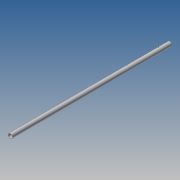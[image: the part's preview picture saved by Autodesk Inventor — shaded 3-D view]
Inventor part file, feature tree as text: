
AUTODESK INVENTOR PART (.ipt)
format: ipt  version: 2016 SP2 (Build 200236200, 236)  size: 98,816 bytes
history: native  units: in
note: dims shown in document units (in); Inventor stores cm internally (conversion verified against a paired STEP export)
features: sketch x3, extrude x2, hole x1
ambient origin geometry x8: Origin, YZ Plane, XZ Plane, XY Plane, X Axis, Y Axis, Z Axis, Center Point
bodies: Solid1 (feature_tree)
feature tree (6):
  extrude  "Extrusion1"  Depth=0.0638in
  extrude  "Extrusion3"  Depth=0.4134in
  hole  "Hole3"  [1 undecoded]
  sketch  "Sketch1"  dims[d0=0.8661in d2=0.0638in]
  sketch  "Sketch6"  dims[d3=29.8819in d4=0.0in d18=0.4134in]
  sketch  "Sketch7"  dims[d19=1.0in d20=0.0in d32=1.1811in d34=5.9055in d35=0.3937in d37=1.0in d39=0.125in d40=0.75in d41=0.375in d42=0.25in d43=0.5635in d44=1.0in d45=0.8108in d47=2.0472in d48=5.9055in]
note: 1 required parameter value undecoded (feature->parameter linkage not recoverable at this tier; creation-order binding heuristic only, values carry confidence <= 0.55)
